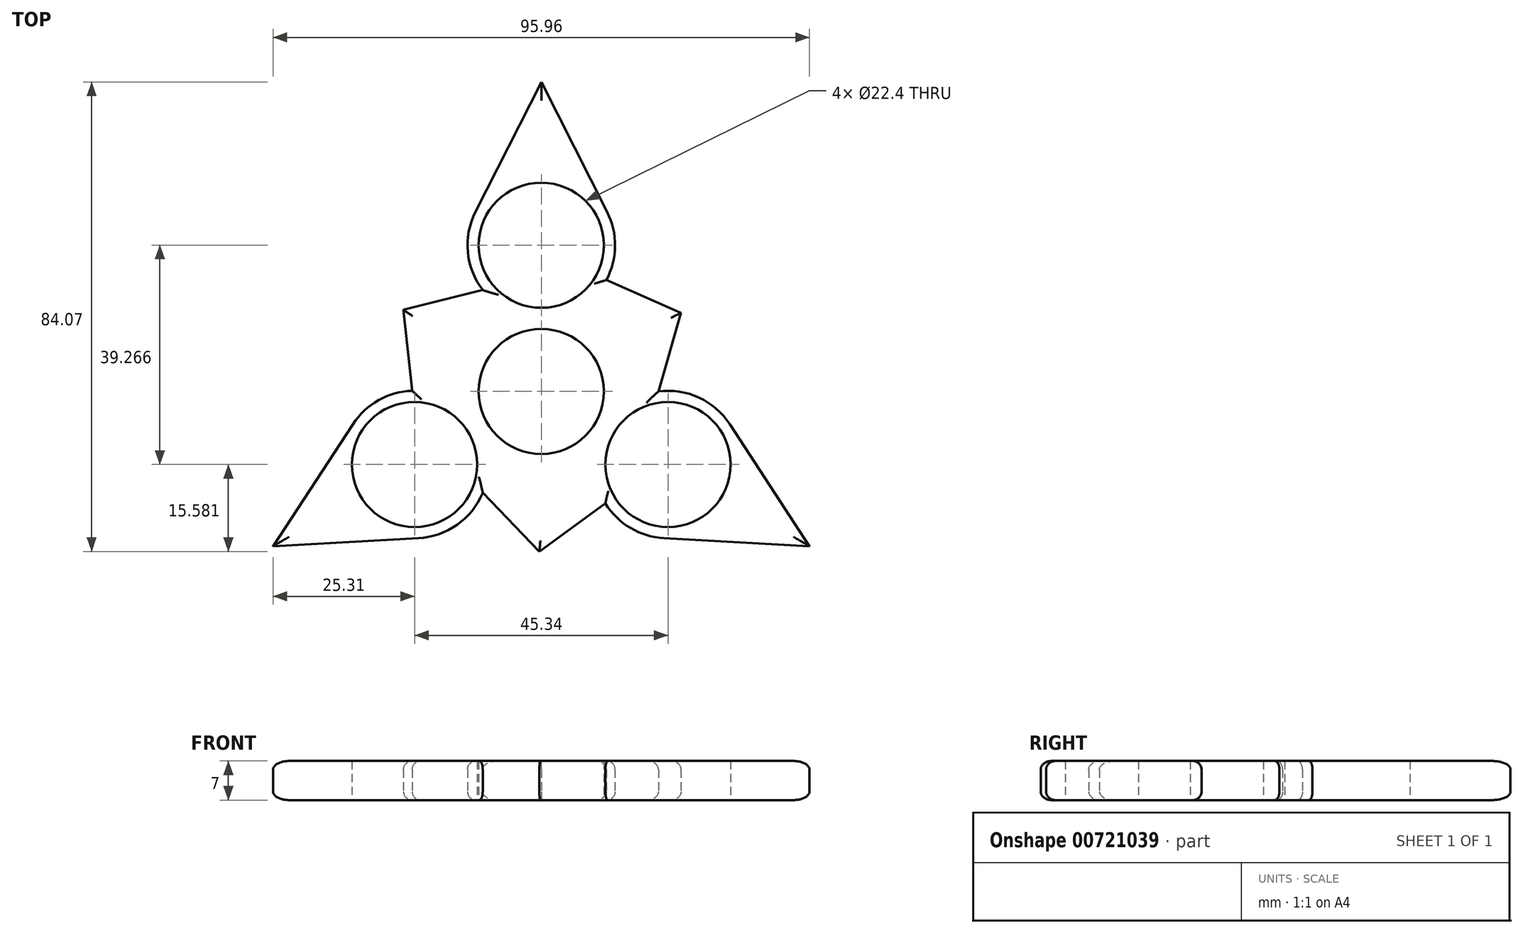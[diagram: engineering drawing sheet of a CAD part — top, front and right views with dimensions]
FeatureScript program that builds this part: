
annotation { "Feature Type Name" : "Feature", "Feature Type Description" : "" }
export const myFeature = defineFeature(function(context is Context, id is Id, definition is map)
    precondition{}
    {
        {
            var Q0;
            Q0=qCreatedBy(makeId("Top.planeOp"),FACE);
            var sketch = newSketch(context, id + "F0", { "sketchPlane" : qUnion([Q0])});
            skCircle(sketch, "E0", {"center": v(0, 0) * mm, "radius": 11.2 * mm});
            skCircle(sketch, "E1", {"center": v(0, 26.18) * mm, "radius": 11.2 * mm});
            skArc(sketch, "E2", {"start": v(11.65, 19.96) * mm, "mid": v(-1.08, 39.33) * mm, "end": v(-10.48, 18.15) * mm});
            skArc(sketch, "E3.1.0", {"start": v(-23.11, 0.1) * mm, "mid": v(-33.52, -20.6) * mm, "end": v(-10.48, -18.15) * mm});
            skCircle(sketch, "E3.1.1", {"center": v(-22.67, -13.09) * mm, "radius": 11.2 * mm});
            skArc(sketch, "E3.2.0", {"start": v(11.47, -20.07) * mm, "mid": v(34.6, -18.73) * mm, "end": v(20.96, 0) * mm});
            skCircle(sketch, "E3.2.1", {"center": v(22.67, -13.09) * mm, "radius": 11.2 * mm});
            skArc(sketch, "E4", {"start": v(11.65, 19.96) * mm, "mid": v(11.76, 7.86) * mm, "end": v(20.96, 0) * mm});
            skArc(sketch, "E5.1.0", {"start": v(-23.11, 0.1) * mm, "mid": v(-12.69, 6.25) * mm, "end": v(-10.48, 18.15) * mm});
            skArc(sketch, "E5.2.0", {"start": v(11.47, -20.07) * mm, "mid": v(0.93, -14.12) * mm, "end": v(-10.48, -18.15) * mm});
            skLineSegment(sketch, "E6", {"start": v(-11.77, 32.16) * mm, "end": v(0, 55.4) * mm});
            skLineSegment(sketch, "E7", {"start": v(0, 55.4) * mm, "end": v(11.78, 32.14) * mm});
            skLineSegment(sketch, "E8.1.0", {"start": v(-47.98, -27.7) * mm, "end": v(-33.72, -5.87) * mm});
            skLineSegment(sketch, "E8.1.1", {"start": v(-21.97, -26.27) * mm, "end": v(-47.98, -27.7) * mm});
            skLineSegment(sketch, "E8.2.0", {"start": v(47.98, -27.7) * mm, "end": v(21.95, -26.27) * mm});
            skLineSegment(sketch, "E8.2.1", {"start": v(33.74, -5.9) * mm, "end": v(47.98, -27.7) * mm});
            skLineSegment(sketch, "E9", {"start": v(-23.11, 0.1) * mm, "end": v(-24.65, 14.63) * mm});
            skLineSegment(sketch, "E10", {"start": v(-24.65, 14.63) * mm, "end": v(-10.48, 18.15) * mm});
            skLineSegment(sketch, "E11.1.0", {"start": v(-0.34, -28.67) * mm, "end": v(-10.48, -18.15) * mm});
            skLineSegment(sketch, "E11.1.1", {"start": v(11.47, -20.07) * mm, "end": v(-0.34, -28.67) * mm});
            skLineSegment(sketch, "E11.2.0", {"start": v(25, 14.04) * mm, "end": v(20.96, 0) * mm});
            skLineSegment(sketch, "E11.2.1", {"start": v(11.65, 19.96) * mm, "end": v(25, 14.04) * mm});
            skSolve(sketch);
        }
        {
            var Q0;
            Q0=qSketchRegion(id+"F0",true);
            extrude(context, id + "F1", {"entities" : qUnion([Q0]), "depth" : 7 * mm, "offsetDistance" : 25 * mm});
        }
        {
            var Q0;
            Q0=makeQuery(id+"F1.opExtrude","CAP_EDGE",EDGE,{"disambiguationData":[OSD([sQuery(id+"F0.wireOp",EDGE,"E11.1.1")])],"isStart":false});
            var Q1;
            Q1=makeQuery(id+"F1.opExtrude","CAP_EDGE",EDGE,{"disambiguationData":[OSD([sQuery(id+"F0.wireOp",EDGE,"E11.1.0")])],"isStart":false});
            var Q2;
            {var subQ0=sQuery(id+"F0.wireOp",EDGE,"E3.1.0");Q2=makeQuery(id+"F1.opExtrude","CAP_EDGE",EDGE,{"disambiguationData":[OSD([subQ0]),TDD([makeQuery(id+"F0.imprint","IMPRINT",EDGE,{"disambiguationData":[TD([[makeQuery(id+"F0.imprint","INTERSECT",VERTEX,{"derivedFrom":[subQ0,sQuery(id+"F0.wireOp",EDGE,"E8.1.1")]}),-1.0]])],"derivedFrom":subQ0})])],"isStart":false});}
            var Q3;
            Q3=makeQuery(id+"F1.opExtrude","CAP_EDGE",EDGE,{"disambiguationData":[OSD([sQuery(id+"F0.wireOp",EDGE,"E8.1.1")])],"isStart":false});
            var Q4;
            Q4=makeQuery(id+"F1.opExtrude","CAP_EDGE",EDGE,{"disambiguationData":[OSD([sQuery(id+"F0.wireOp",EDGE,"E8.1.0")])],"isStart":false});
            var Q5;
            {var subQ0=sQuery(id+"F0.wireOp",EDGE,"E3.1.0");Q5=makeQuery(id+"F1.opExtrude","CAP_EDGE",EDGE,{"disambiguationData":[OSD([subQ0]),TDD([makeQuery(id+"F0.imprint","IMPRINT",EDGE,{"disambiguationData":[TD([[makeQuery(id+"F0.imprint","INTERSECT",VERTEX,{"derivedFrom":[subQ0,sQuery(id+"F0.wireOp",EDGE,"E8.1.0")]}),1.0]])],"derivedFrom":subQ0})])],"isStart":false});}
            var Q6;
            Q6=makeQuery(id+"F1.opExtrude","CAP_EDGE",EDGE,{"disambiguationData":[OSD([sQuery(id+"F0.wireOp",EDGE,"E9")])],"isStart":false});
            var Q7;
            Q7=makeQuery(id+"F1.opExtrude","CAP_EDGE",EDGE,{"disambiguationData":[OSD([sQuery(id+"F0.wireOp",EDGE,"E10")])],"isStart":false});
            var Q8;
            {var subQ0=sQuery(id+"F0.wireOp",EDGE,"E2");Q8=makeQuery(id+"F1.opExtrude","CAP_EDGE",EDGE,{"disambiguationData":[OSD([subQ0]),TDD([makeQuery(id+"F0.imprint","IMPRINT",EDGE,{"disambiguationData":[TD([[makeQuery(id+"F0.imprint","INTERSECT",VERTEX,{"derivedFrom":[subQ0,sQuery(id+"F0.wireOp",EDGE,"E6")]}),-1.0]])],"derivedFrom":subQ0})])],"isStart":false});}
            var Q9;
            Q9=makeQuery(id+"F1.opExtrude","CAP_EDGE",EDGE,{"disambiguationData":[OSD([sQuery(id+"F0.wireOp",EDGE,"E6")])],"isStart":false});
            var Q10;
            {var subQ0=sQuery(id+"F0.wireOp",EDGE,"E3.2.0");Q10=makeQuery(id+"F1.opExtrude","CAP_EDGE",EDGE,{"disambiguationData":[OSD([subQ0]),TDD([makeQuery(id+"F0.imprint","IMPRINT",EDGE,{"disambiguationData":[TD([[makeQuery(id+"F0.imprint","INTERSECT",VERTEX,{"derivedFrom":[subQ0,sQuery(id+"F0.wireOp",EDGE,"E8.2.0")]}),1.0]])],"derivedFrom":subQ0})])],"isStart":false});}
            var Q11;
            Q11=makeQuery(id+"F1.opExtrude","CAP_EDGE",EDGE,{"disambiguationData":[OSD([sQuery(id+"F0.wireOp",EDGE,"E8.2.0")])],"isStart":false});
            var Q12;
            Q12=makeQuery(id+"F1.opExtrude","CAP_EDGE",EDGE,{"disambiguationData":[OSD([sQuery(id+"F0.wireOp",EDGE,"E8.2.1")])],"isStart":false});
            var Q13;
            {var subQ0=sQuery(id+"F0.wireOp",EDGE,"E3.2.0");Q13=makeQuery(id+"F1.opExtrude","CAP_EDGE",EDGE,{"disambiguationData":[OSD([subQ0]),TDD([makeQuery(id+"F0.imprint","IMPRINT",EDGE,{"disambiguationData":[TD([[makeQuery(id+"F0.imprint","INTERSECT",VERTEX,{"derivedFrom":[subQ0,sQuery(id+"F0.wireOp",EDGE,"E8.2.1")]}),-1.0]])],"derivedFrom":subQ0})])],"isStart":false});}
            var Q14;
            Q14=makeQuery(id+"F1.opExtrude","CAP_EDGE",EDGE,{"disambiguationData":[OSD([sQuery(id+"F0.wireOp",EDGE,"E11.2.0")])],"isStart":false});
            var Q15;
            Q15=makeQuery(id+"F1.opExtrude","CAP_EDGE",EDGE,{"disambiguationData":[OSD([sQuery(id+"F0.wireOp",EDGE,"E11.2.1")])],"isStart":false});
            var Q16;
            {var subQ0=sQuery(id+"F0.wireOp",EDGE,"E2");Q16=makeQuery(id+"F1.opExtrude","CAP_EDGE",EDGE,{"disambiguationData":[OSD([subQ0]),TDD([makeQuery(id+"F0.imprint","IMPRINT",EDGE,{"disambiguationData":[TD([[makeQuery(id+"F0.imprint","INTERSECT",VERTEX,{"derivedFrom":[subQ0,sQuery(id+"F0.wireOp",EDGE,"E7")]}),1.0]])],"derivedFrom":subQ0})])],"isStart":false});}
            var Q17;
            Q17=makeQuery(id+"F1.opExtrude","CAP_EDGE",EDGE,{"disambiguationData":[OSD([sQuery(id+"F0.wireOp",EDGE,"E7")])],"isStart":true});
            var Q18;
            Q18=makeQuery(id+"F1.opExtrude","CAP_EDGE",EDGE,{"disambiguationData":[OSD([sQuery(id+"F0.wireOp",EDGE,"E8.1.0")])],"isStart":true});
            var Q19;
            {var subQ0=sQuery(id+"F0.wireOp",EDGE,"E3.1.0");Q19=makeQuery(id+"F1.opExtrude","CAP_EDGE",EDGE,{"disambiguationData":[OSD([subQ0]),TDD([makeQuery(id+"F0.imprint","IMPRINT",EDGE,{"disambiguationData":[TD([[makeQuery(id+"F0.imprint","INTERSECT",VERTEX,{"derivedFrom":[subQ0,sQuery(id+"F0.wireOp",EDGE,"E8.1.0")]}),1.0]])],"derivedFrom":subQ0})])],"isStart":true});}
            var Q20;
            Q20=makeQuery(id+"F1.opExtrude","CAP_EDGE",EDGE,{"disambiguationData":[OSD([sQuery(id+"F0.wireOp",EDGE,"E9")])],"isStart":true});
            var Q21;
            Q21=makeQuery(id+"F1.opExtrude","CAP_EDGE",EDGE,{"disambiguationData":[OSD([sQuery(id+"F0.wireOp",EDGE,"E10")])],"isStart":true});
            var Q22;
            {var subQ0=sQuery(id+"F0.wireOp",EDGE,"E2");Q22=makeQuery(id+"F1.opExtrude","CAP_EDGE",EDGE,{"disambiguationData":[OSD([subQ0]),TDD([makeQuery(id+"F0.imprint","IMPRINT",EDGE,{"disambiguationData":[TD([[makeQuery(id+"F0.imprint","INTERSECT",VERTEX,{"derivedFrom":[subQ0,sQuery(id+"F0.wireOp",EDGE,"E6")]}),-1.0]])],"derivedFrom":subQ0})])],"isStart":true});}
            var Q23;
            Q23=makeQuery(id+"F1.opExtrude","CAP_EDGE",EDGE,{"disambiguationData":[OSD([sQuery(id+"F0.wireOp",EDGE,"E6")])],"isStart":true});
            var Q24;
            Q24=makeQuery(id+"F1.opExtrude","CAP_EDGE",EDGE,{"disambiguationData":[OSD([sQuery(id+"F0.wireOp",EDGE,"E8.1.1")])],"isStart":true});
            var Q25;
            {var subQ0=sQuery(id+"F0.wireOp",EDGE,"E3.1.0");Q25=makeQuery(id+"F1.opExtrude","CAP_EDGE",EDGE,{"disambiguationData":[OSD([subQ0]),TDD([makeQuery(id+"F0.imprint","IMPRINT",EDGE,{"disambiguationData":[TD([[makeQuery(id+"F0.imprint","INTERSECT",VERTEX,{"derivedFrom":[subQ0,sQuery(id+"F0.wireOp",EDGE,"E8.1.1")]}),-1.0]])],"derivedFrom":subQ0})])],"isStart":true});}
            var Q26;
            Q26=makeQuery(id+"F1.opExtrude","CAP_EDGE",EDGE,{"disambiguationData":[OSD([sQuery(id+"F0.wireOp",EDGE,"E11.1.1")])],"isStart":true});
            var Q27;
            Q27=makeQuery(id+"F1.opExtrude","CAP_EDGE",EDGE,{"disambiguationData":[OSD([sQuery(id+"F0.wireOp",EDGE,"E11.2.0")])],"isStart":true});
            var Q28;
            Q28=makeQuery(id+"F1.opExtrude","CAP_EDGE",EDGE,{"disambiguationData":[OSD([sQuery(id+"F0.wireOp",EDGE,"E8.2.1")])],"isStart":true});
            var Q29;
            {var subQ0=sQuery(id+"F0.wireOp",EDGE,"E2");Q29=makeQuery(id+"F1.opExtrude","CAP_EDGE",EDGE,{"disambiguationData":[OSD([subQ0]),TDD([makeQuery(id+"F0.imprint","IMPRINT",EDGE,{"disambiguationData":[TD([[makeQuery(id+"F0.imprint","INTERSECT",VERTEX,{"derivedFrom":[subQ0,sQuery(id+"F0.wireOp",EDGE,"E7")]}),1.0]])],"derivedFrom":subQ0})])],"isStart":true});}
            var Q30;
            {var subQ0=sQuery(id+"F0.wireOp",EDGE,"E3.2.0");Q30=makeQuery(id+"F1.opExtrude","CAP_EDGE",EDGE,{"disambiguationData":[OSD([subQ0]),TDD([makeQuery(id+"F0.imprint","IMPRINT",EDGE,{"disambiguationData":[TD([[makeQuery(id+"F0.imprint","INTERSECT",VERTEX,{"derivedFrom":[subQ0,sQuery(id+"F0.wireOp",EDGE,"E8.2.1")]}),-1.0]])],"derivedFrom":subQ0})])],"isStart":true});}
            var Q31;
            Q31=makeQuery(id+"F1.opExtrude","CAP_EDGE",EDGE,{"disambiguationData":[OSD([sQuery(id+"F0.wireOp",EDGE,"E8.2.0")])],"isStart":true});
            var Q32;
            Q32=makeQuery(id+"F1.opExtrude","CAP_EDGE",EDGE,{"disambiguationData":[OSD([sQuery(id+"F0.wireOp",EDGE,"E11.2.1")])],"isStart":true});
            var Q33;
            Q33=makeQuery(id+"F1.opExtrude","CAP_EDGE",EDGE,{"disambiguationData":[OSD([sQuery(id+"F0.wireOp",EDGE,"E11.1.0")])],"isStart":true});
            fillet(context, id + "F2", {"entities" : qUnion([Q0, Q1, Q2, Q3, Q4, Q5, Q6, Q7, Q8, Q9, Q10, Q11, Q12, Q13, Q14, Q15, Q16, Q17, Q18, Q19, Q20, Q21, Q22, Q23, Q24, Q25, Q26, Q27, Q28, Q29, Q30, Q31, Q32, Q33]), "radius" : 1.5 * mm, "tangentPropagation" : true, "allowEdgeOverflow" : false});
        }
    });
